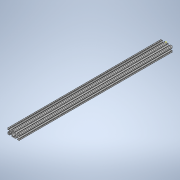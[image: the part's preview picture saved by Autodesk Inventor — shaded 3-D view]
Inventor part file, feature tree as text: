
AUTODESK INVENTOR PART (.ipt)
format: ipt  version: 2020 (Build 240168000, 168)  size: 329,216 bytes
history: native  units: in
note: dims shown in document units (in); Inventor stores cm internally (conversion verified against a paired STEP export)
features: sketch x2, extrude x1
ambient origin geometry x8: Origin, YZ Plane, XZ Plane, XY Plane, X Axis, Y Axis, Z Axis, Center Point
bodies: Solid1 (feature_tree)
feature tree (3):
  extrude  "Extrusion1"  [1 undecoded]
  sketch  "Sketch2"
  sketch  "Sketch1"  dims[d0=26.0in d1=0.0in]
note: 1 required parameter value undecoded (feature->parameter linkage not recoverable at this tier; creation-order binding heuristic only, values carry confidence <= 0.55)
